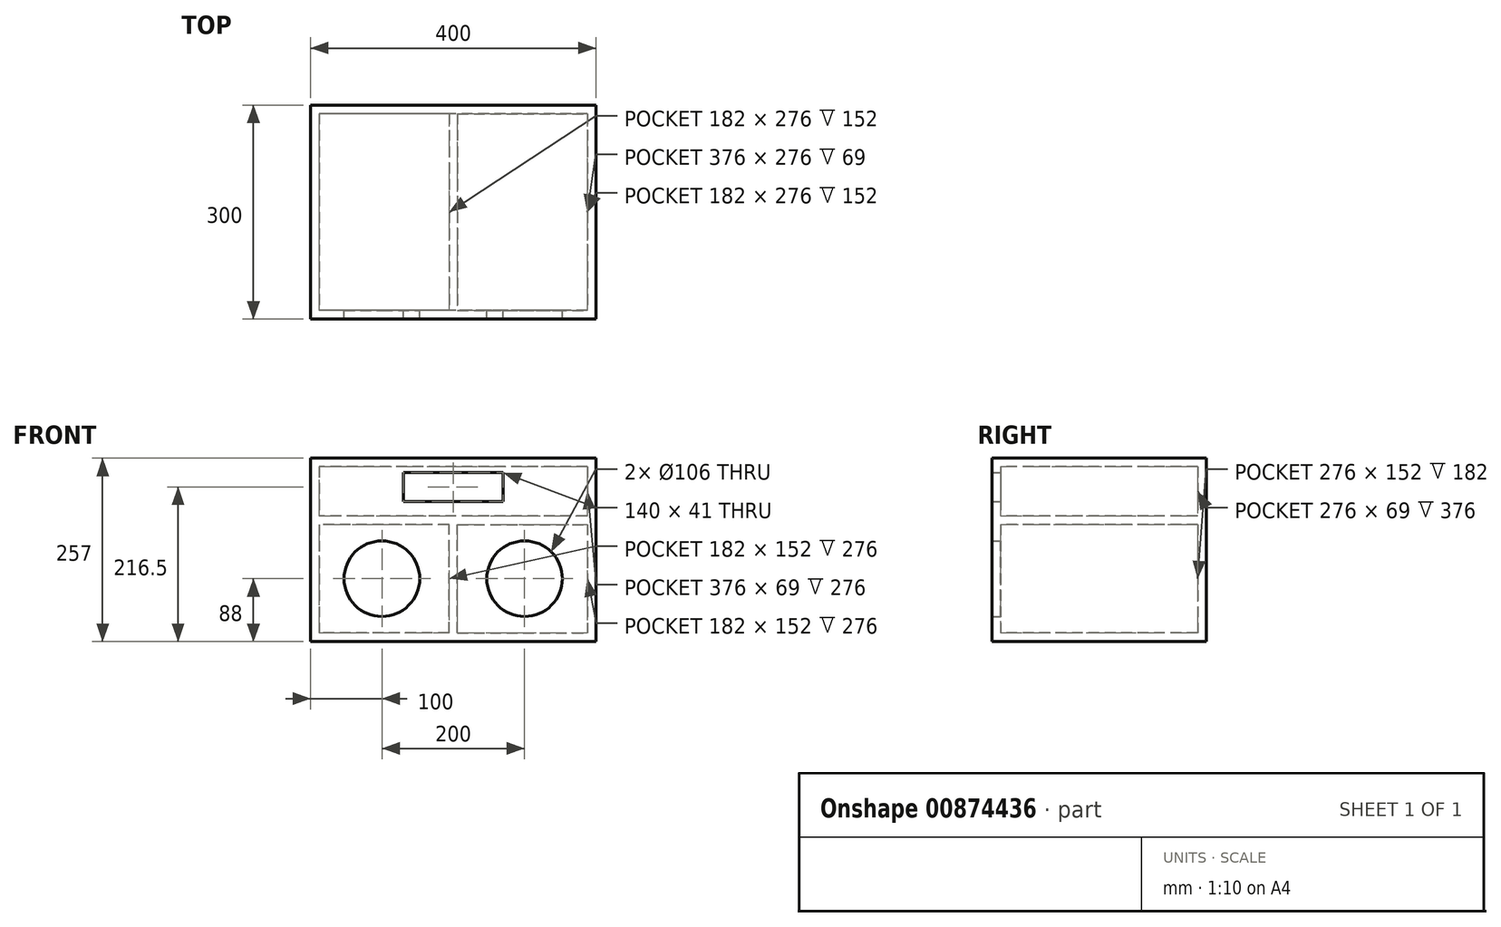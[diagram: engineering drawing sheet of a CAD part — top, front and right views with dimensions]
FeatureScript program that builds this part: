
annotation { "Feature Type Name" : "Feature", "Feature Type Description" : "" }
export const myFeature = defineFeature(function(context is Context, id is Id, definition is map)
    precondition{}
    {
        {
            var Q0;
            Q0=qCreatedBy(makeId("Front.planeOp"),FACE);
            var sketch = newSketch(context, id + "F0", { "sketchPlane" : qUnion([Q0])});
            skLineSegment(sketch, "E0.bottom", {"start": v(-100, 128.5) * mm, "end": v(100, 128.5) * mm});
            skLineSegment(sketch, "E0.top", {"start": v(-100, -128.5) * mm, "end": v(100, -128.5) * mm});
            skLineSegment(sketch, "E0.left", {"start": v(-100, 128.5) * mm, "end": v(-100, -128.5) * mm});
            skLineSegment(sketch, "E0.right", {"start": v(100, 128.5) * mm, "end": v(100, -128.5) * mm});
            skPoint(sketch, "E0.middle", {"position": v(0, 0) * mm});
            skCircle(sketch, "E1", {"center": v(0, -40.5) * mm, "radius": 53 * mm});
            skLineSegment(sketch, "E2.bottom", {"start": v(100, 108.5) * mm, "end": v(30, 108.5) * mm});
            skLineSegment(sketch, "E2.top", {"start": v(100, 67.5) * mm, "end": v(30, 67.5) * mm});
            skLineSegment(sketch, "E2.left", {"start": v(100, 108.5) * mm, "end": v(100, 67.5) * mm});
            skLineSegment(sketch, "E2.right", {"start": v(30, 108.5) * mm, "end": v(30, 67.5) * mm});
            skLineSegment(sketch, "E3.bottom", {"start": v(-100, 47.5) * mm, "end": v(100, 47.5) * mm});
            skLineSegment(sketch, "E3.top", {"start": v(-100, 35.5) * mm, "end": v(100, 35.5) * mm});
            skLineSegment(sketch, "E3.left", {"start": v(-100, 47.5) * mm, "end": v(-100, 35.5) * mm});
            skLineSegment(sketch, "E3.right", {"start": v(100, 47.5) * mm, "end": v(100, 35.5) * mm});
            skCircle(sketch, "E4", {"center": v(0, -40.5) * mm, "radius": 67 * mm});
            skSolve(sketch);
        }
        {
            var Q0;
            {var subQ1=sQuery(id+"F0.wireOp",EDGE,"E0.top");Q0=makeQuery(id+"F0.imprint","IMPRINT",FACE,{"disambiguationData":[TD([[makeQuery(id+"F0.imprint","IMPRINT",EDGE,{"derivedFrom":subQ1}),1.0]])]});}
            var Q1;
            {var subQ1=sQuery(id+"F0.wireOp",EDGE,"E0.bottom");Q1=makeQuery(id+"F0.imprint","IMPRINT",FACE,{"disambiguationData":[TD([[makeQuery(id+"F0.imprint","IMPRINT",EDGE,{"derivedFrom":subQ1}),-1.0]])]});}
            var Q2;
            Q2=makeQuery(id+"F0.imprint","IMPRINT",FACE,{"disambiguationData":[TD([[makeQuery(id+"F0.imprint","IMPRINT",EDGE,{"derivedFrom":sQuery(id+"F0.wireOp",EDGE,"E3.bottom")}),-1.0]])]});
            var Q3;
            Q3=makeQuery(id+"F0.imprint","IMPRINT",FACE,{"disambiguationData":[TD([[makeQuery(id+"F0.imprint","IMPRINT",EDGE,{"derivedFrom":sQuery(id+"F0.wireOp",EDGE,"E1")}),-1.0]])]});
            extrude(context, id + "F1", {"entities" : qUnion([Q0, Q1, Q2, Q3]), "depth" : 12 * mm, "offsetDistance" : 25 * mm});
        }
        {
            var Q0;
            Q0=makeQuery(id+"F1.opExtrude","CAP_FACE",FACE,{"disambiguationData":[OSD([sQuery(id+"F0.wireOp",EDGE,"E0.bottom"),sQuery(id+"F0.wireOp",EDGE,"E0.top"),sQuery(id+"F0.wireOp",EDGE,"E0.left"),sQuery(id+"F0.wireOp",EDGE,"E0.right"),sQuery(id+"F0.wireOp",EDGE,"E1"),sQuery(id+"F0.wireOp",EDGE,"E2.bottom"),sQuery(id+"F0.wireOp",EDGE,"E2.top"),sQuery(id+"F0.wireOp",EDGE,"E2.right"),sQuery(id+"F0.wireOp",EDGE,"E3.left"),sQuery(id+"F0.wireOp",EDGE,"E3.right")])],"isStart":true});
            var sketch = newSketch(context, id + "F2", { "sketchPlane" : qUnion([Q0])});
            skLineSegment(sketch, "E5.bottom", {"start": v(-100, 128.5) * mm, "end": v(100, 128.5) * mm});
            skLineSegment(sketch, "E5.top", {"start": v(-100, 116.5) * mm, "end": v(100, 116.5) * mm});
            skLineSegment(sketch, "E5.left", {"start": v(-100, 128.5) * mm, "end": v(-100, 116.5) * mm});
            skLineSegment(sketch, "E5.right", {"start": v(100, 128.5) * mm, "end": v(100, 116.5) * mm});
            skLineSegment(sketch, "E6.bottom", {"start": v(-100, -128.5) * mm, "end": v(100, -128.5) * mm});
            skLineSegment(sketch, "E6.top", {"start": v(-100, -116.5) * mm, "end": v(100, -116.5) * mm});
            skLineSegment(sketch, "E6.left", {"start": v(-100, -128.5) * mm, "end": v(-100, -116.5) * mm});
            skLineSegment(sketch, "E6.right", {"start": v(100, -128.5) * mm, "end": v(100, -116.5) * mm});
            skLineSegment(sketch, "E7.bottom", {"start": v(100, 116.5) * mm, "end": v(88, 116.5) * mm});
            skLineSegment(sketch, "E7.top", {"start": v(100, -116.5) * mm, "end": v(88, -116.5) * mm});
            skLineSegment(sketch, "E7.left", {"start": v(100, 116.5) * mm, "end": v(100, -116.5) * mm});
            skLineSegment(sketch, "E7.right", {"start": v(88, 116.5) * mm, "end": v(88, -116.5) * mm});
            skLineSegment(sketch, "E8.bottom", {"start": v(-100, -116.5) * mm, "end": v(-94, -116.5) * mm});
            skLineSegment(sketch, "E8.top", {"start": v(-100, 35.5) * mm, "end": v(-94, 35.5) * mm});
            skLineSegment(sketch, "E8.left", {"start": v(-100, -116.5) * mm, "end": v(-100, 35.5) * mm});
            skLineSegment(sketch, "E8.right", {"start": v(-94, -116.5) * mm, "end": v(-94, 35.5) * mm});
            skLineSegment(sketch, "E9.bottom", {"start": v(-100, 35.5) * mm, "end": v(100, 35.5) * mm});
            skLineSegment(sketch, "E9.top", {"start": v(-100, 47.5) * mm, "end": v(100, 47.5) * mm});
            skLineSegment(sketch, "E9.left", {"start": v(-100, 35.5) * mm, "end": v(-100, 47.5) * mm});
            skLineSegment(sketch, "E9.right", {"start": v(100, 35.5) * mm, "end": v(100, 47.5) * mm});
            skSolve(sketch);
        }
        {
            var Q0;
            Q0 = qSketchRegion(id + "F2", true);
            extrude(context, id + "F3", {"entities" : qUnion([Q0]), "operationType" : NewBodyOperationType.ADD, "depth" : 276 * mm, "offsetDistance" : 25 * mm});
        }
        {
            var Q0;
            Q0=makeQuery(id+"F3.opExtrude","CAP_FACE",FACE,{"disambiguationData":[OSD([sQuery(id+"F2.wireOp",EDGE,"E5.bottom"),sQuery(id+"F2.wireOp",EDGE,"E5.top"),sQuery(id+"F2.wireOp",EDGE,"E5.left"),sQuery(id+"F2.wireOp",EDGE,"E5.right"),sQuery(id+"F2.wireOp",EDGE,"E6.bottom"),sQuery(id+"F2.wireOp",EDGE,"E6.top"),sQuery(id+"F2.wireOp",EDGE,"E6.left"),sQuery(id+"F2.wireOp",EDGE,"E6.right"),sQuery(id+"F2.wireOp",EDGE,"E7.left"),sQuery(id+"F2.wireOp",EDGE,"E7.right"),sQuery(id+"F2.wireOp",EDGE,"E8.left"),sQuery(id+"F2.wireOp",EDGE,"E8.right"),sQuery(id+"F2.wireOp",EDGE,"E9.bottom"),sQuery(id+"F2.wireOp",EDGE,"E9.top"),sQuery(id+"F2.wireOp",EDGE,"E9.left"),sQuery(id+"F2.wireOp",EDGE,"E9.right")])],"isStart":false});
            var sketch = newSketch(context, id + "F4", { "sketchPlane" : qUnion([Q0])});
            skLineSegment(sketch, "E10.bottom", {"start": v(100, 128.5) * mm, "end": v(-100, 128.5) * mm});
            skLineSegment(sketch, "E10.top", {"start": v(100, -128.5) * mm, "end": v(-100, -128.5) * mm});
            skLineSegment(sketch, "E10.left", {"start": v(100, 128.5) * mm, "end": v(100, -128.5) * mm});
            skLineSegment(sketch, "E10.right", {"start": v(-100, 128.5) * mm, "end": v(-100, -128.5) * mm});
            skSolve(sketch);
        }
        {
            var Q0;
            Q0 = qSketchRegion(id + "F4", true);
            extrude(context, id + "F5", {"entities" : qUnion([Q0]), "operationType" : NewBodyOperationType.ADD, "depth" : 12 * mm, "offsetDistance" : 25 * mm});
        }
        {
            var Q0;
            Q0=makeQuery(id+"F1.opExtrude","SWEPT_BODY",BODY,{"disambiguationData":[OSD([sQuery(id+"F0.wireOp",EDGE,"E0.bottom"),sQuery(id+"F0.wireOp",EDGE,"E0.top"),sQuery(id+"F0.wireOp",EDGE,"E0.left"),sQuery(id+"F0.wireOp",EDGE,"E0.right"),sQuery(id+"F0.wireOp",EDGE,"E1"),sQuery(id+"F0.wireOp",EDGE,"E2.bottom"),sQuery(id+"F0.wireOp",EDGE,"E2.top"),sQuery(id+"F0.wireOp",EDGE,"E2.right"),sQuery(id+"F0.wireOp",EDGE,"E3.left"),sQuery(id+"F0.wireOp",EDGE,"E3.right")])]});
            var Q1;
            {var subQ0=sQuery(id+"F0.wireOp",EDGE,"E0.right");Q1=makeQuery(id+"F5.boolean.opBoolean","MERGE",FACE,{"derivedFrom":[makeQuery(id+"F3.boolean.opBoolean","MERGE",FACE,{"derivedFrom":[makeQuery(id+"F1.opExtrude","SWEPT_FACE",FACE,{"disambiguationData":[OSD([subQ0])]}),makeQuery(id+"F3.opExtrude","SWEPT_FACE",FACE,{"disambiguationData":[OSD([sQuery(id+"F2.wireOp",EDGE,"E5.left")])]})]}),makeQuery(id+"F3.boolean.opBoolean","MERGE",FACE,{"derivedFrom":[makeQuery(id+"F1.opExtrude","SWEPT_FACE",FACE,{"disambiguationData":[OSD([subQ0,sQuery(id+"F0.wireOp",EDGE,"E3.right")])]}),makeQuery(id+"F3.opExtrude","SWEPT_FACE",FACE,{"disambiguationData":[OSD([sQuery(id+"F2.wireOp",EDGE,"E6.left"),sQuery(id+"F2.wireOp",EDGE,"E8.left"),sQuery(id+"F2.wireOp",EDGE,"E9.left")])]})]}),makeQuery(id+"F5.opExtrude","SWEPT_FACE",FACE,{"disambiguationData":[OSD([sQuery(id+"F4.wireOp",EDGE,"E10.right")])]})]});}
            mirror(context, id + "F6", {"operationType" : NewBodyOperationType.ADD, "entities" : qUnion([Q0]), "mirrorPlane" : qUnion([Q1])});
        }
    });
